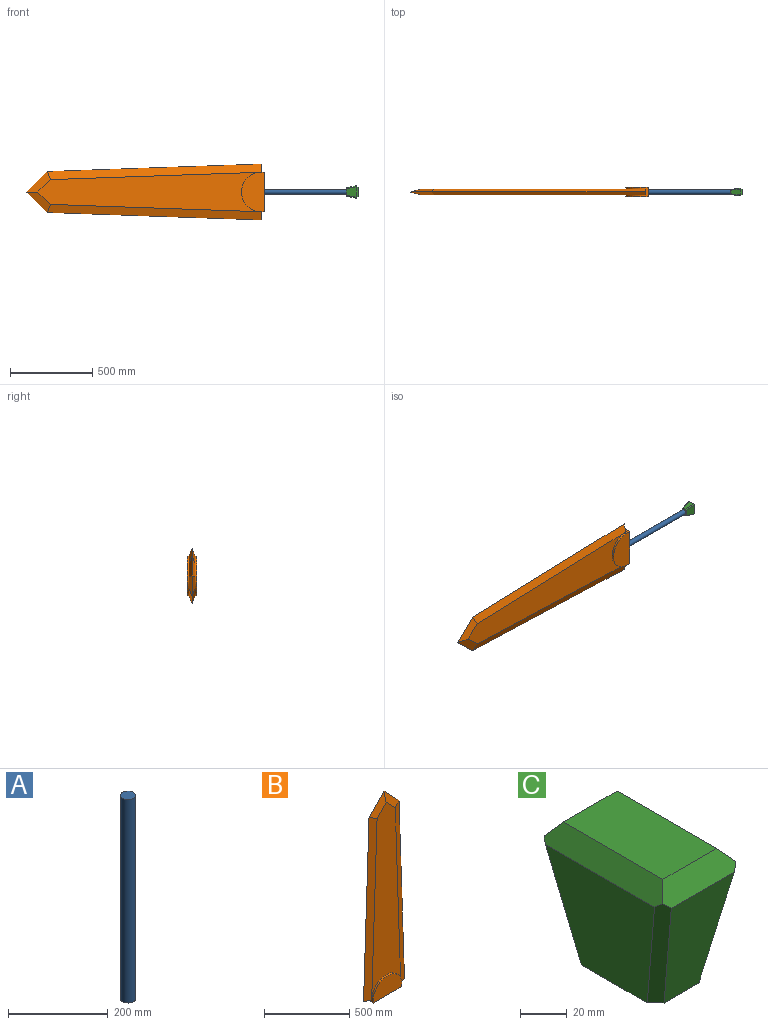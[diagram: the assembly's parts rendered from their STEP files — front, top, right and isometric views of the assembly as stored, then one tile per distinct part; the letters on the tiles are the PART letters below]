
ASSEMBLY  parts=3 mates=2
PART A: 3 faces, bbox 30x30x500 mm
  f0: cylinder r=15mm len=500mm, axis (0,0,1), area 47123.9mm2, adj f1,f2
  f1: plane 30x30mm, normal (0,0,1), area 706.9mm2, adj f0
  f2: plane 30x30mm, normal (0,0,-1), area 706.9mm2, adj f0
PART B: 21 faces, bbox 338.9x60x1446.7 mm
  f0: cylinder r=120mm len=237.41mm, axis (0,-1,0), area 4100.1mm2, adj f1,f2,f4,f9
  f1: plane 60x35.19mm, normal (1,0,0), area 2111.2mm2, adj f0,f3,f4,f5,f14,f15
  f2: plane 60x35.19mm, normal (-1,0,0), area 2111.2mm2, adj f0,f3,f4,f7,f14,f15
  f3: plane 237.41x60mm, normal (0,0,-1), area 14244.4mm2, adj f1,f2,f4,f15
  f4: plane 237.41x137.59mm, normal (0,-1,0), area 26765.8mm2, adj f0,f1,f2,f3
  f5: cylinder r=120mm len=36mm, axis (0,-1,0), area 635.2mm2, adj f1,f8,f9,f10,f16,f17
  f6: plane 49.45x35.98mm, normal (0,0,-1), area 889.6mm2, adj f7,f11,f18
  f7: cylinder r=120mm len=36mm, axis (0,-1,0), area 635.2mm2, adj f2,f6,f9,f11,f16,f18
  f8: plane 49.45x35.98mm, normal (0,0,-1), area 889.6mm2, adj f5,f10,f17
  f9: plane 1348.51x239.3mm, normal (0,-1,0), area 233075.8mm2, adj f0,f5,f7,f10,f11,f12,f13
  f10: plane 1299.77x94.15mm, normal (0.34,-0.94,0.01), area 67903.6mm2, adj f5,f8,f9,f12,f17
  f11: plane 1299.77x94.15mm, normal (-0.34,-0.94,0.01), area 67903.6mm2, adj f6,f7,f9,f13,f18
  f12: plane 149.94x124.07mm, normal (0.25,-0.94,0.24), area 7578.5mm2, adj f9,f10,f13,f19
  f13: plane 149.94x124.07mm, normal (-0.25,-0.94,0.24), area 7578.5mm2, adj f9,f11,f12,f20
  f14: cylinder r=120mm len=237.41mm, axis (0,1,0), area 4100.1mm2, adj f1,f2,f15,f16
  f15: plane 237.41x137.59mm, normal (0,1,0), area 26765.8mm2, adj f1,f2,f3,f14
  f16: plane 1348.51x239.3mm, normal (0,1,0), area 233075.8mm2, adj f5,f7,f14,f17,f18,f19,f20
  f17: plane 1299.77x94.15mm, normal (0.34,0.94,0.01), area 67903.6mm2, adj f5,f8,f10,f16,f19
  f18: plane 1299.77x94.15mm, normal (-0.34,0.94,0.01), area 67903.6mm2, adj f6,f7,f11,f16,f20
  f19: plane 149.94x124.07mm, normal (0.25,0.94,0.24), area 7578.5mm2, adj f12,f16,f17,f20
  f20: plane 149.94x124.07mm, normal (-0.25,0.94,0.24), area 7578.5mm2, adj f13,f16,f18,f19
PART C: 14 faces, bbox 48.4x75.8x70 mm
  f0: plane 50x31mm, normal (0,0,-1), area 1498.4mm2, adj f2,f3,f4,f5,f10,f11,f12,f13
  f1: plane 60x32.36mm, normal (0,0,1), area 1941.5mm2, adj f6,f7,f8,f9
  f2: plane 65.82x60.77mm, normal (-0.99,0,-0.14), area 3241.4mm2, adj f0,f7,f12,f13
  f3: plane 60.22x38.11mm, normal (0,-0.98,-0.21), area 1817.3mm2, adj f0,f9,f11,f12
  f4: plane 65.82x60.77mm, normal (0.99,0,-0.14), area 3241.4mm2, adj f0,f8,f10,f11
  f5: plane 60.22x38.11mm, normal (0,0.98,-0.21), area 1817.3mm2, adj f0,f6,f10,f13
  f6: plane 44.51x9.78mm, normal (0,0.78,0.63), area 493.5mm2, adj f1,f5,f7,f8,f10,f13
  f7: plane 71.32x9.23mm, normal (-0.76,0,0.66), area 810.6mm2, adj f1,f2,f6,f9,f12,f13
  f8: plane 71.32x9.23mm, normal (0.76,0,0.66), area 810.6mm2, adj f1,f4,f6,f9,f10,f11
  f9: plane 44.51x9.78mm, normal (0,-0.78,0.63), area 493.5mm2, adj f1,f3,f7,f8,f11,f12
  f10: plane 63x18.02mm, normal (0.69,0.68,-0.24), area 457.4mm2, adj f0,f4,f5,f6,f8
  f11: plane 63x18.02mm, normal (0.69,-0.68,-0.24), area 457.4mm2, adj f0,f3,f4,f8,f9
  f12: plane 63x18.02mm, normal (-0.69,-0.68,-0.24), area 457.4mm2, adj f0,f2,f3,f7,f9
  f13: plane 63x18.02mm, normal (-0.69,0.68,-0.24), area 457.4mm2, adj f0,f2,f5,f6,f7
PLACE A rot(axis=(-0.58,-0.58,0.58),120deg) t=(500,0,0)mm
PLACE B rot(axis=(0,-1,0),90deg) t=(-17.59,0,0)mm
PLACE C rot(axis=(-0.58,0.58,-0.58),120deg) t=(500,0,0)mm
MATE fastened B.f3 <-> A.f0  axis (1,0,0) through (0,0,0)mm
MATE fastened C.f0 <-> A.f0  axis (-1,0,0) through (500,0,0)mm
